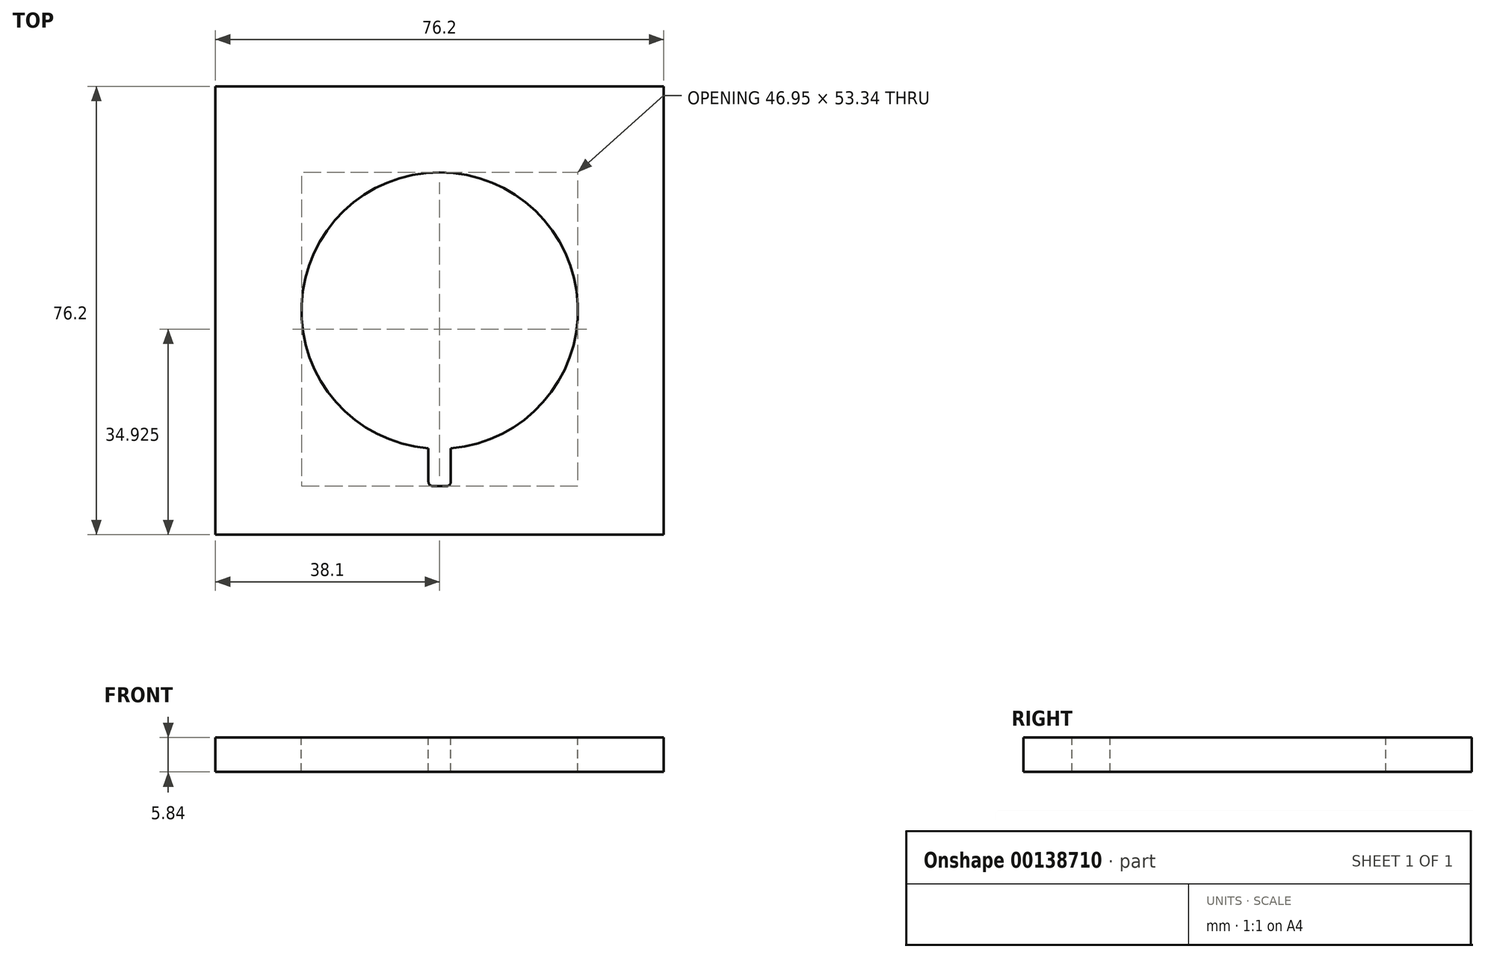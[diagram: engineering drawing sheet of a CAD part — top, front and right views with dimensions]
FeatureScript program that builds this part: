
annotation { "Feature Type Name" : "Feature", "Feature Type Description" : "" }
export const myFeature = defineFeature(function(context is Context, id is Id, definition is map)
    precondition{}
    {
        {
            var Q0;
            Q0=qCreatedBy(makeId("Top.planeOp"),FACE);
            var sketch = newSketch(context, id + "F0", { "sketchPlane" : qUnion([Q0])});
            skLineSegment(sketch, "E0.bottom", {"start": v(0, 0) * mm, "end": v(-76.2, 0) * mm});
            skLineSegment(sketch, "E0.top", {"start": v(0, 76.2) * mm, "end": v(-76.2, 76.2) * mm});
            skLineSegment(sketch, "E0.left", {"start": v(0, 0) * mm, "end": v(0, 76.2) * mm});
            skLineSegment(sketch, "E0.right", {"start": v(-76.2, 0) * mm, "end": v(-76.2, 76.2) * mm});
            skSolve(sketch);
        }
        {
            var Q0;
            Q0=makeQuery(id+"F0.imprint","IMPRINT",FACE,{"disambiguationData":[TD([[makeQuery(id+"F0.imprint","IMPRINT",EDGE,{"derivedFrom":sQuery(id+"F0.wireOp",EDGE,"E0.bottom")}),-1.0]])]});
            extrude(context, id + "F1", {"entities" : qUnion([Q0]), "depth" : 5.84 * mm});
        }
        {
            var Q0;
            Q0=makeQuery(id+"F1.opExtrude","CAP_FACE",FACE,{"disambiguationData":[OSD([sQuery(id+"F0.wireOp",EDGE,"E0.bottom"),sQuery(id+"F0.wireOp",EDGE,"E0.top"),sQuery(id+"F0.wireOp",EDGE,"E0.left"),sQuery(id+"F0.wireOp",EDGE,"E0.right")])],"isStart":false});
            var sketch = newSketch(context, id + "F2", { "sketchPlane" : qUnion([Q0])});
            skCircle(sketch, "E1", {"center": v(-38.1, 38.1) * mm, "radius": 23.5 * mm});
            skPoint(sketch, "E2", {"position": v(-76.2, 38.1) * mm});
            skPoint(sketch, "E3", {"position": v(-38.1, 76.2) * mm});
            skLineSegment(sketch, "E4.bottom", {"start": v(-40, 38.1) * mm, "end": v(-36.2, 38.1) * mm});
            skLineSegment(sketch, "E4.top", {"start": v(-39.24, 8.25) * mm, "end": v(-36.96, 8.25) * mm});
            skLineSegment(sketch, "E4.left", {"start": v(-40, 38.1) * mm, "end": v(-40, 9.02) * mm});
            skLineSegment(sketch, "E4.right", {"start": v(-36.2, 38.1) * mm, "end": v(-36.2, 9.02) * mm});
            skPoint(sketch, "E5", {"position": v(-38.1, 14.6) * mm});
            skPoint(sketch, "E6.visualSharp", {"position": v(-40, 8.26) * mm});
            skArc(sketch, "E6.filletArc", {"start": v(-40, 9.02) * mm, "mid": v(-39.78, 8.48) * mm, "end": v(-39.24, 8.26) * mm});
            skPoint(sketch, "E7.visualSharp", {"position": v(-36.2, 8.26) * mm});
            skArc(sketch, "E7.filletArc", {"start": v(-36.96, 8.26) * mm, "mid": v(-36.42, 8.48) * mm, "end": v(-36.2, 9.02) * mm});
            skSolve(sketch);
        }
        {
            var Q0;
            Q0=makeQuery(id+"F2.imprint","IMPRINT",FACE,{"disambiguationData":[TD([[makeQuery(id+"F2.imprint","IMPRINT",EDGE,{"derivedFrom":sQuery(id+"F2.wireOp",EDGE,"E4.top")}),1.0]])]});
            var Q1;
            {var subQ5=sQuery(id+"F2.wireOp",EDGE,"E4.bottom");Q1=makeQuery(id+"F2.imprint","IMPRINT",FACE,{"disambiguationData":[TD([[makeQuery(id+"F2.imprint","IMPRINT",EDGE,{"derivedFrom":subQ5}),-1.0]])]});}
            var Q2;
            {var subQ5=sQuery(id+"F2.wireOp",EDGE,"E4.bottom");Q2=makeQuery(id+"F2.imprint","IMPRINT",FACE,{"disambiguationData":[TD([[makeQuery(id+"F2.imprint","IMPRINT",EDGE,{"derivedFrom":subQ5}),1.0]])]});}
            var Q3;
            Q3=makeQuery(id+"F1.opExtrude","CAP_FACE",FACE,{"disambiguationData":[OSD([sQuery(id+"F0.wireOp",EDGE,"E0.bottom"),sQuery(id+"F0.wireOp",EDGE,"E0.top"),sQuery(id+"F0.wireOp",EDGE,"E0.left"),sQuery(id+"F0.wireOp",EDGE,"E0.right")])],"isStart":true});
            extrude(context, id + "F3", {"entities" : qUnion([Q0, Q1, Q2]), "operationType" : NewBodyOperationType.REMOVE, "endBound" : BoundingType.UP_TO_SURFACE, "oppositeDirection" : true, "endBoundEntityFace" : qUnion([Q3]), "depth" : 25.4 * mm});
        }
    });
